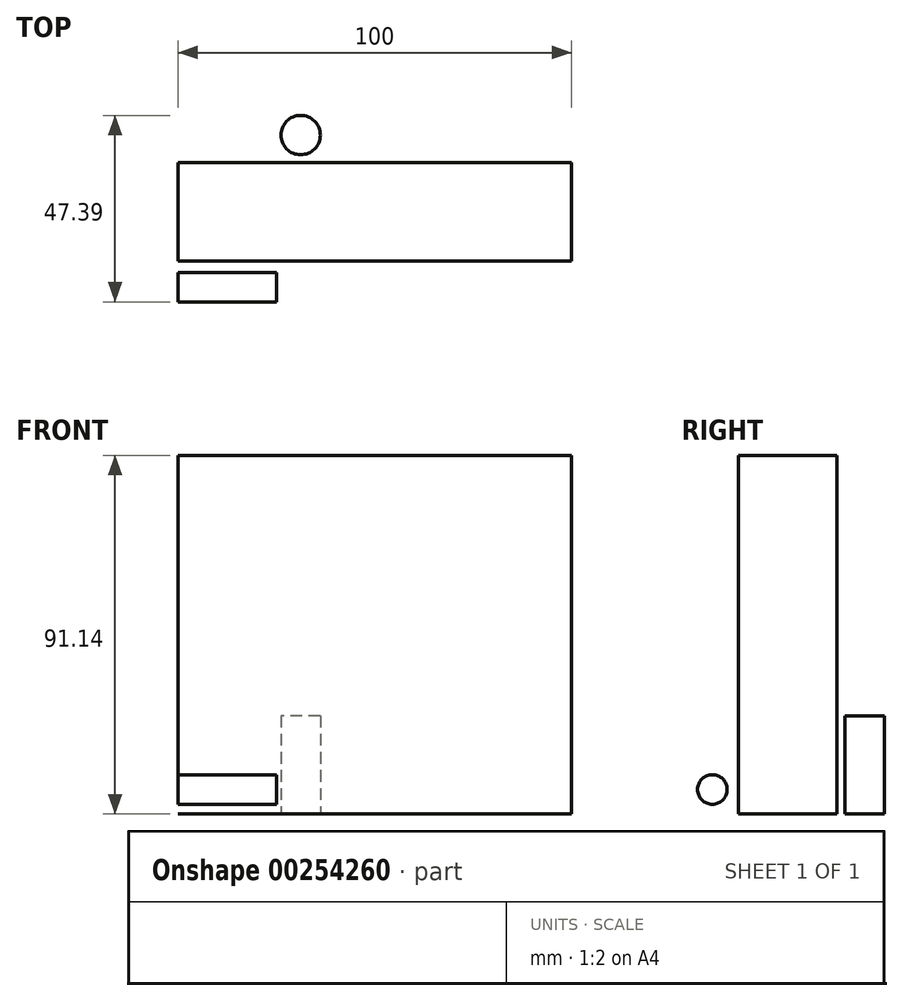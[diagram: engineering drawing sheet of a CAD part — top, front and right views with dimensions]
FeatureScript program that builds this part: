
annotation { "Feature Type Name" : "Feature", "Feature Type Description" : "" }
export const myFeature = defineFeature(function(context is Context, id is Id, definition is map)
    precondition{}
    {
        {
            var Q0;
            Q0=qCreatedBy(makeId("Front.planeOp"),FACE);
            var sketch = newSketch(context, id + "F0", { "sketchPlane" : qUnion([Q0])});
            skLineSegment(sketch, "E0.bottom", {"start": v(0, 0) * mm, "end": v(100, 0) * mm});
            skLineSegment(sketch, "E0.top", {"start": v(0, 91.14) * mm, "end": v(100, 91.14) * mm});
            skLineSegment(sketch, "E0.left", {"start": v(0, 0) * mm, "end": v(0, 91.14) * mm});
            skLineSegment(sketch, "E0.right", {"start": v(100, 0) * mm, "end": v(100, 91.14) * mm});
            skSolve(sketch);
        }
        {
            var Q0;
            Q0 = qSketchRegion(id + "F0", true);
            extrude(context, id + "F1", {"entities" : qUnion([Q0]), "depth" : 25 * mm});
        }
        {
            var Q0;
            Q0=qCreatedBy(makeId("Top.planeOp"),FACE);
            var sketch = newSketch(context, id + "F2", { "sketchPlane" : qUnion([Q0])});
            skCircle(sketch, "E1", {"center": v(31.15, 7) * mm, "radius": 5 * mm});
            skSolve(sketch);
        }
        {
            var Q0;
            Q0 = qSketchRegion(id + "F2", true);
            extrude(context, id + "F3", {"entities" : qUnion([Q0]), "depth" : 25 * mm});
        }
        {
            var Q0;
            Q0=qCreatedBy(makeId("Right.planeOp"),FACE);
            var sketch = newSketch(context, id + "F4", { "sketchPlane" : qUnion([Q0])});
            skCircle(sketch, "E2", {"center": v(-31.66, 6.26) * mm, "radius": 3.74 * mm});
            skSolve(sketch);
        }
        {
            var Q0;
            Q0 = qSketchRegion(id + "F4", true);
            extrude(context, id + "F5", {"entities" : qUnion([Q0]), "depth" : 25 * mm});
        }
    });
